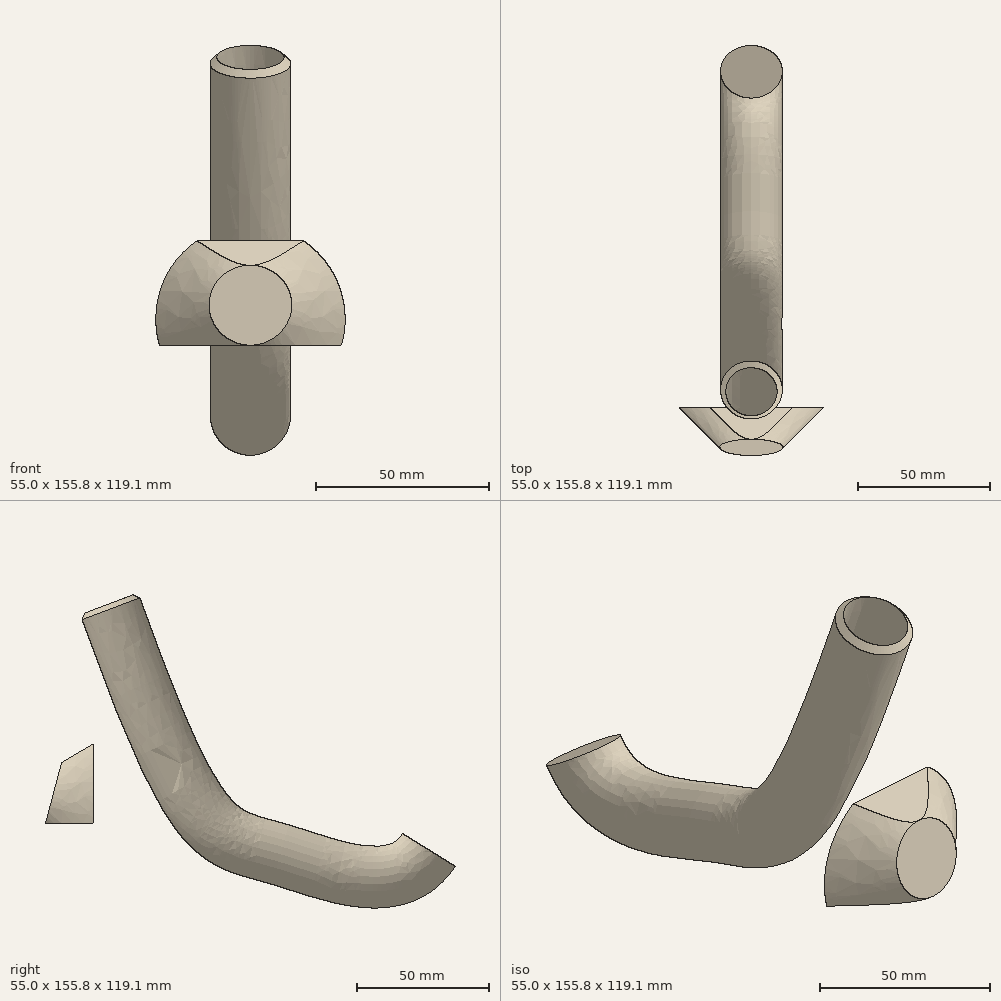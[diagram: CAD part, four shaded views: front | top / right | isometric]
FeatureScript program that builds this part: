
annotation { "Feature Type Name" : "Feature", "Feature Type Description" : "" }
export const myFeature = defineFeature(function(context is Context, id is Id, definition is map)
    precondition{}
    {
        {
            var Q0;
            Q0=qCreatedBy(makeId("Right.planeOp"),FACE);
            var sketch = newSketch(context, id + "F0", { "sketchPlane" : qUnion([Q0])});
            skLineSegment(sketch, "E0", {"start": v(-64.16, 20.98) * mm, "end": v(-125.1, -85.6) * mm, "construction": true});
            skLineSegment(sketch, "E1", {"start": v(-81.61, -9.55) * mm, "end": v(-81.61, -54.55) * mm, "construction": true});
            skLineSegment(sketch, "E2", {"start": v(-81.61, -54.55) * mm, "end": v(-16.95, -54.55) * mm, "construction": true});
            skLineSegment(sketch, "E3", {"start": v(-22.12, 37.03) * mm, "end": v(-49.28, -10.48) * mm, "construction": true});
            skPoint(sketch, "E3.endSnap0", {"position": v(-49.28, -54.55) * mm});
            skLineSegment(sketch, "E4", {"start": v(-64.16, 20.98) * mm, "end": v(-22.12, 37.03) * mm, "construction": true});
            skPoint(sketch, "E5", {"position": v(-43.14, 29) * mm});
            skLineSegment(sketch, "E6", {"start": v(-54.12, 24.81) * mm, "end": v(-32.17, 33.2) * mm});
            skPoint(sketch, "E7", {"position": v(-31.47, -9.55) * mm});
            skLineSegment(sketch, "E8", {"start": v(-49.28, -54.55) * mm, "end": v(-49.28, -39.55) * mm});
            skLineSegment(sketch, "E9", {"start": v(-61.21, -31.35) * mm, "end": v(-67.35, -54.55) * mm});
            skLineSegment(sketch, "E10", {"start": v(-28.48, -9.55) * mm, "end": v(-43.14, 29) * mm});
            skLineSegment(sketch, "E11", {"start": v(-28.48, -9.55) * mm, "end": v(-64.28, -42.95) * mm});
            skLineSegment(sketch, "E12", {"start": v(-64.28, -42.95) * mm, "end": v(-49.28, -47.05) * mm});
            skLineSegment(sketch, "E13", {"start": v(24.12, 15.33) * mm, "end": v(24.12, -88.01) * mm, "construction": true});
            skLineSegment(sketch, "E14", {"start": v(-39.71, -13.76) * mm, "end": v(-17.24, -5.33) * mm});
            skLineSegment(sketch, "E15", {"start": v(-32.17, 33.2) * mm, "end": v(-17.24, -5.33) * mm});
            skLineSegment(sketch, "E16", {"start": v(-17.24, -5.33) * mm, "end": v(-61.21, -31.35) * mm});
            skLineSegment(sketch, "E17", {"start": v(-49.28, -74.55) * mm, "end": v(-49.28, -19.55) * mm});
            skLineSegment(sketch, "E18", {"start": v(-61.21, -31.35) * mm, "end": v(-49.28, -19.55) * mm});
            skLineSegment(sketch, "E19", {"start": v(-54.12, 24.81) * mm, "end": v(-39.71, -13.76) * mm});
            skLineSegment(sketch, "E20", {"start": v(-39.71, -13.76) * mm, "end": v(-67.35, -54.55) * mm});
            skLineSegment(sketch, "E21", {"start": v(-67.35, -54.55) * mm, "end": v(-49.28, -74.55) * mm});
            skLineSegment(sketch, "E22", {"start": v(-61.21, -31.35) * mm, "end": v(-49.28, -39.55) * mm});
            skLineSegment(sketch, "E23", {"start": v(-67.35, -54.55) * mm, "end": v(-49.28, -54.55) * mm});
            skLineSegment(sketch, "E24", {"start": v(-49.28, -19.55) * mm, "end": v(34.44, -19.55) * mm});
            skLineSegment(sketch, "E25", {"start": v(34.44, -19.55) * mm, "end": v(34.44, -74.55) * mm});
            skLineSegment(sketch, "E26", {"start": v(34.44, -74.55) * mm, "end": v(-49.28, -74.55) * mm});
            skSolve(sketch);
        }
        {
            var Q0;
            Q0=sQuery(id+"F0.wireOp",EDGE,"E6");
            cPlane(context, id + "F1", {"entities" : qUnion([Q0]), "cplaneType" : CPlaneType.LINE_ANGLE, "offset" : 150 * mm, "angle" : 0 * degree, "width" : 150 * mm, "height" : 150 * mm});
        }
        {
            var Q0;
            Q0=sQuery(id+"F0.wireOp",EDGE,"E14");
            cPlane(context, id + "F2", {"entities" : qUnion([Q0]), "cplaneType" : CPlaneType.LINE_ANGLE, "offset" : 150 * mm, "angle" : 0 * degree, "width" : 150 * mm, "height" : 150 * mm});
        }
        {
            var Q0;
            Q0=sQuery(id+"F0.wireOp",EDGE,"E9");
            cPlane(context, id + "F3", {"entities" : qUnion([Q0]), "cplaneType" : CPlaneType.LINE_ANGLE, "offset" : 150 * mm, "angle" : 90 * degree, "width" : 150 * mm, "height" : 150 * mm});
        }
        {
            var Q0;
            Q0=sQuery(id+"F0.wireOp",EDGE,"E8");
            cPlane(context, id + "F4", {"entities" : qUnion([Q0]), "cplaneType" : CPlaneType.LINE_ANGLE, "offset" : 150 * mm, "angle" : 90 * degree, "width" : 150 * mm, "height" : 150 * mm});
        }
        {
            var Q0;
            Q0=qCreatedBy(id+"F1.planeOp",FACE);
            var sketch = newSketch(context, id + "F5", { "sketchPlane" : qUnion([Q0])});
            skCircle(sketch, "E27", {"center": v(0, -29.96) * mm, "radius": 11.75 * mm});
            skSolve(sketch);
        }
        {
            var Q0;
            Q0=qCreatedBy(id+"F3.planeOp",FACE);
            var sketch = newSketch(context, id + "F6", { "sketchPlane" : qUnion([Q0])});
            skCircle(sketch, "E28", {"center": v(0, -57.97) * mm, "radius": 12 * mm});
            skSolve(sketch);
        }
        {
            var Q0;
            Q0=qCreatedBy(id+"F4.planeOp",FACE);
            var sketch = newSketch(context, id + "F7", { "sketchPlane" : qUnion([Q0])});
            skCircle(sketch, "E29", {"center": v(0, -47.05) * mm, "radius": 27.5 * mm});
            skSolve(sketch);
        }
        {
            var Q0;
            Q0=qCreatedBy(makeId("Right.planeOp"),FACE);
            var sketch = newSketch(context, id + "F8", { "sketchPlane" : qUnion([Q0])});
            skFitSpline(sketch, "E30", {"points": [v(-43.14, 29) * mm, v(22.14, -66.27) * mm, v(78.43, -64.52) * mm], "startDerivative": vector(171.23, -478.6) * mm, "endDerivative": vector(89.59, 137.72) * mm});
            skSolve(sketch);
        }
        {
            var Q0;
            Q0=makeQuery(id+"F5.imprint","IMPRINT",FACE,{"disambiguationData":[TD([[makeQuery(id+"F5.imprint","IMPRINT",EDGE,{"derivedFrom":sQuery(id+"F5.wireOp",EDGE,"E27")}),1.0]])]});
            var Q1;
            Q1=sQuery(id+"F8.wireOp",EDGE,"E30");
            sweep(context, id + "F9", {"profiles" : qUnion([Q0]), "path" : qUnion([Q1])});
        }
        {
            var Q1;
            Q1=makeQuery(id+"F7.imprint","IMPRINT",FACE,{"disambiguationData":[TD([[makeQuery(id+"F7.imprint","IMPRINT",EDGE,{"derivedFrom":sQuery(id+"F7.wireOp",EDGE,"E29")}),1.0]])]});
            var Q2;
            Q2=makeQuery(id+"F6.imprint","IMPRINT",FACE,{"disambiguationData":[TD([[makeQuery(id+"F6.imprint","IMPRINT",EDGE,{"derivedFrom":sQuery(id+"F6.wireOp",EDGE,"E28")}),1.0]])]});
            loft(context, id + "F10", {"operationType" : NewBodyOperationType.ADD, "sheetProfilesArray" : [{ "sheetProfileEntities" : qUnion([Q1]) }, { "sheetProfileEntities" : qUnion([Q2]) }]});
        }
        {
            var Q0;
            {var subQ1=sQuery(id+"F0.wireOp",EDGE,"E18");Q0=makeQuery(id+"F0.imprint","IMPRINT",FACE,{"disambiguationData":[TD([[makeQuery(id+"F0.imprint","IMPRINT",EDGE,{"derivedFrom":subQ1}),-1.0]])]});}
            var Q1;
            {var subQ1=sQuery(id+"F0.wireOp",EDGE,"E21");Q1=makeQuery(id+"F0.imprint","IMPRINT",FACE,{"disambiguationData":[TD([[makeQuery(id+"F0.imprint","IMPRINT",EDGE,{"derivedFrom":subQ1}),1.0]])]});}
            var Q2;
            {var subQ1=sQuery(id+"F0.wireOp",EDGE,"E24");Q2=makeQuery(id+"F0.imprint","IMPRINT",FACE,{"disambiguationData":[TD([[makeQuery(id+"F0.imprint","IMPRINT",EDGE,{"derivedFrom":subQ1}),-1.0]])]});}
            extrude(context, id + "F11", {"entities" : qUnion([Q0, Q1, Q2]), "operationType" : NewBodyOperationType.REMOVE, "endBound" : BoundingType.SYMMETRIC, "oppositeDirection" : true, "depth" : 60 * mm});
        }
        {
            var Q0;
            Q0=makeQuery(id+"F11.boolean.opBoolean","COPY",FACE,{"derivedFrom":makeQuery(id+"F11.opExtrude","SWEPT_FACE",FACE,{"disambiguationData":[OSD([sQuery(id+"F0.wireOp",EDGE,"E22")])]})});
            var Q1;
            Q1=makeQuery(id+"F11.boolean.opBoolean","MERGE",FACE,{"derivedFrom":[makeQuery(id+"F10.opLoft","CAP_FACE",FACE,{"disambiguationData":[OSD([makeQuery(id+"F7.imprint","IMPRINT",FACE,{"disambiguationData":[TD([[makeQuery(id+"F7.imprint","IMPRINT",EDGE,{"derivedFrom":sQuery(id+"F7.wireOp",EDGE,"E29")}),1.0]])]})])],"isStart":true}),makeQuery(id+"F11.opExtrude","SWEPT_FACE",FACE,{"disambiguationData":[OSD([sQuery(id+"F0.wireOp",EDGE,"E17")])]})]});
            var Q2;
            Q2=makeQuery(id+"F11.boolean.opBoolean","COPY",FACE,{"derivedFrom":makeQuery(id+"F11.opExtrude","SWEPT_FACE",FACE,{"disambiguationData":[OSD([sQuery(id+"F0.wireOp",EDGE,"E23")])]})});
            var Q3;
            Q3=makeQuery(id+"F9.opSweep","CAP_FACE",FACE,{"disambiguationData":[OSD([sQuery(id+"F5.wireOp",EDGE,"E27"),sQuery(id+"F8.wireOp",VERTEX,"E30.start")])],"isStart":true});
            shell(context, id + "F12", {"entities" : qUnion([Q0, Q1, Q2, Q3]), "thickness" : 2 * mm});
        }
        {
            var Q0;
            Q0=makeQuery(id+"F9.opSweep","CAP_EDGE",EDGE,{"disambiguationData":[OSD([sQuery(id+"F5.wireOp",EDGE,"E27"),sQuery(id+"F8.wireOp",VERTEX,"E30.start")])],"isStart":true});
            chamfer(context, id + "F13", {"entities" : qUnion([Q0]), "width" : 2 * mm, "tangentPropagation" : true});
        }
    });
